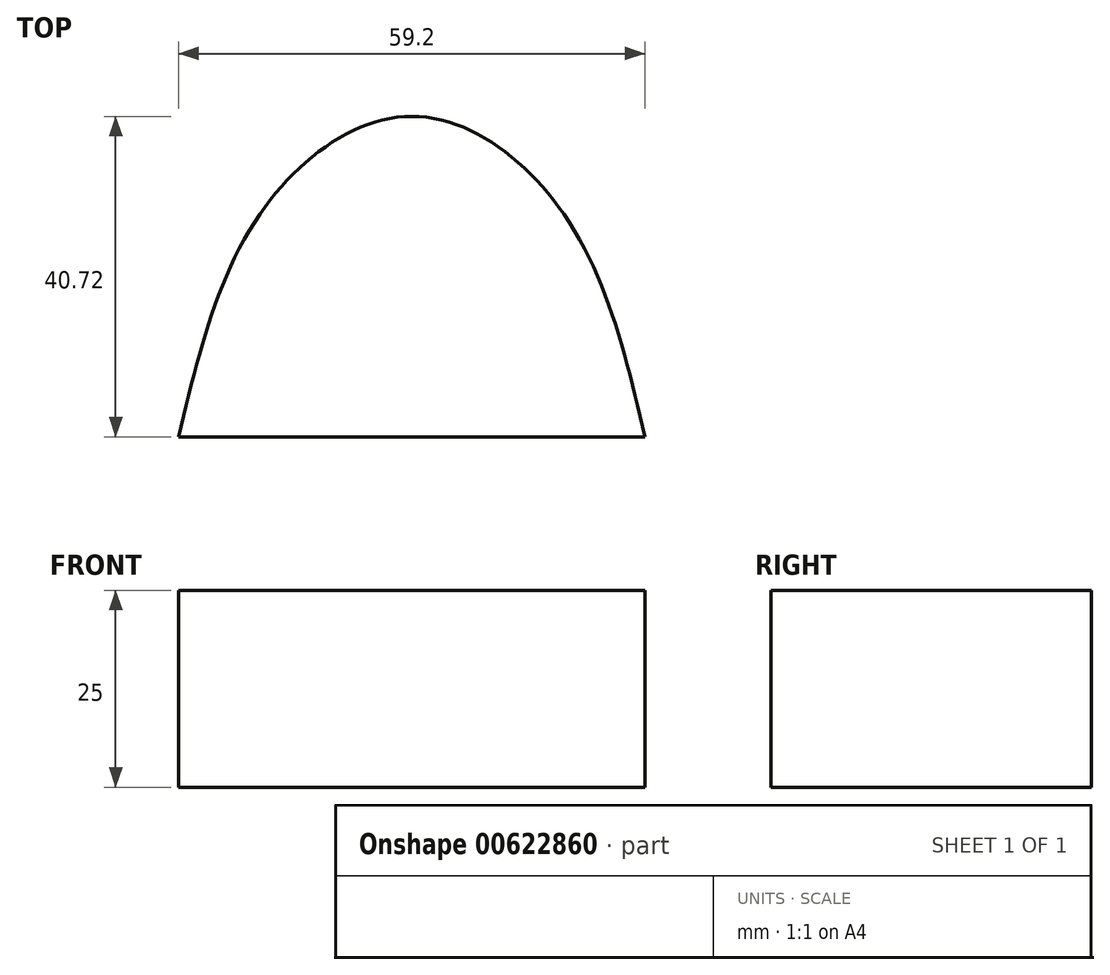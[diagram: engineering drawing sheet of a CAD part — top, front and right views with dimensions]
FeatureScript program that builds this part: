
annotation { "Feature Type Name" : "Feature", "Feature Type Description" : "" }
export const myFeature = defineFeature(function(context is Context, id is Id, definition is map)
    precondition{}
    {
        {
            var Q0;
            Q0=qCreatedBy(makeId("Top.planeOp"),FACE);
            var sketch = newSketch(context, id + "F0", { "sketchPlane" : qUnion([Q0])});
            skLineSegment(sketch, "E0", {"start": v(0, -20.36) * mm, "end": v(29.6, -20.36) * mm});
            skLineSegment(sketch, "E1", {"start": v(0, -20.36) * mm, "end": v(0, 20.36) * mm});
            skLineSegment(sketch, "E2", {"start": v(0, 20.36) * mm, "end": v(19.3, 7.94) * mm});
            skLineSegment(sketch, "E3", {"start": v(19.3, 7.94) * mm, "end": v(29.6, -20.36) * mm});
            skLineSegment(sketch, "E4", {"start": v(19.3, 7.94) * mm, "end": v(0, 7.94) * mm});
            skLineSegment(sketch, "E5.MirrorCS", {"start": v(0, -20.36) * mm, "end": v(-29.6, -20.36) * mm});
            skLineSegment(sketch, "E6.MirrorCS", {"start": v(-19.3, 7.94) * mm, "end": v(-29.6, -20.36) * mm});
            skLineSegment(sketch, "E7.MirrorCS", {"start": v(0, 20.36) * mm, "end": v(-19.3, 7.94) * mm});
            skFitSpline(sketch, "E8", {"points": [v(29.6, -20.36) * mm, v(19.3, 7.94) * mm, v(0, 20.36) * mm, v(-19.3, 7.94) * mm, v(-29.6, -20.36) * mm], "startDerivative": vector(-26.77, 113.89) * mm, "endDerivative": vector(-26.77, -113.89) * mm});
            skSolve(sketch);
        }
        {
            var Q0;
            {var subQ0=sQuery(id+"F0.wireOp",EDGE,"E2");Q0=makeQuery(id+"F0.imprint","IMPRINT",FACE,{"disambiguationData":[TD([[makeQuery(id+"F0.imprint","IMPRINT",EDGE,{"derivedFrom":subQ0}),1.0]])]});}
            var Q1;
            {var subQ0=sQuery(id+"F0.wireOp",EDGE,"E3");Q1=makeQuery(id+"F0.imprint","IMPRINT",FACE,{"disambiguationData":[TD([[makeQuery(id+"F0.imprint","IMPRINT",EDGE,{"derivedFrom":subQ0}),1.0]])]});}
            var Q2;
            {var subQ0=sQuery(id+"F0.wireOp",EDGE,"E7.MirrorCS");Q2=makeQuery(id+"F0.imprint","IMPRINT",FACE,{"disambiguationData":[TD([[makeQuery(id+"F0.imprint","IMPRINT",EDGE,{"derivedFrom":subQ0}),-1.0]])]});}
            var Q3;
            {var subQ0=sQuery(id+"F0.wireOp",EDGE,"E6.MirrorCS");Q3=makeQuery(id+"F0.imprint","IMPRINT",FACE,{"disambiguationData":[TD([[makeQuery(id+"F0.imprint","IMPRINT",EDGE,{"derivedFrom":subQ0}),-1.0]])]});}
            var Q4;
            {var subQ3=sQuery(id+"F0.wireOp",EDGE,"E5.MirrorCS");Q4=makeQuery(id+"F0.imprint","IMPRINT",FACE,{"disambiguationData":[TD([[makeQuery(id+"F0.imprint","IMPRINT",EDGE,{"derivedFrom":subQ3}),-1.0]])]});}
            var Q5;
            {var subQ0=sQuery(id+"F0.wireOp",EDGE,"E0");Q5=makeQuery(id+"F0.imprint","IMPRINT",FACE,{"disambiguationData":[TD([[makeQuery(id+"F0.imprint","IMPRINT",EDGE,{"derivedFrom":subQ0}),1.0]])]});}
            var Q6;
            {var subQ0=sQuery(id+"F0.wireOp",EDGE,"E2");Q6=makeQuery(id+"F0.imprint","IMPRINT",FACE,{"disambiguationData":[TD([[makeQuery(id+"F0.imprint","IMPRINT",EDGE,{"derivedFrom":subQ0}),-1.0]])]});}
            var Q7;
            Q7=sQuery(id+"F0.wireOp",EDGE,"E8");
            extrude(context, id + "F1", {"entities" : qUnion([Q0, Q1, Q2, Q3, Q4, Q5, Q6]), "surfaceEntities" : qUnion([Q7]), "depth" : 25 * mm, "offsetDistance" : 25 * mm});
        }
    });
